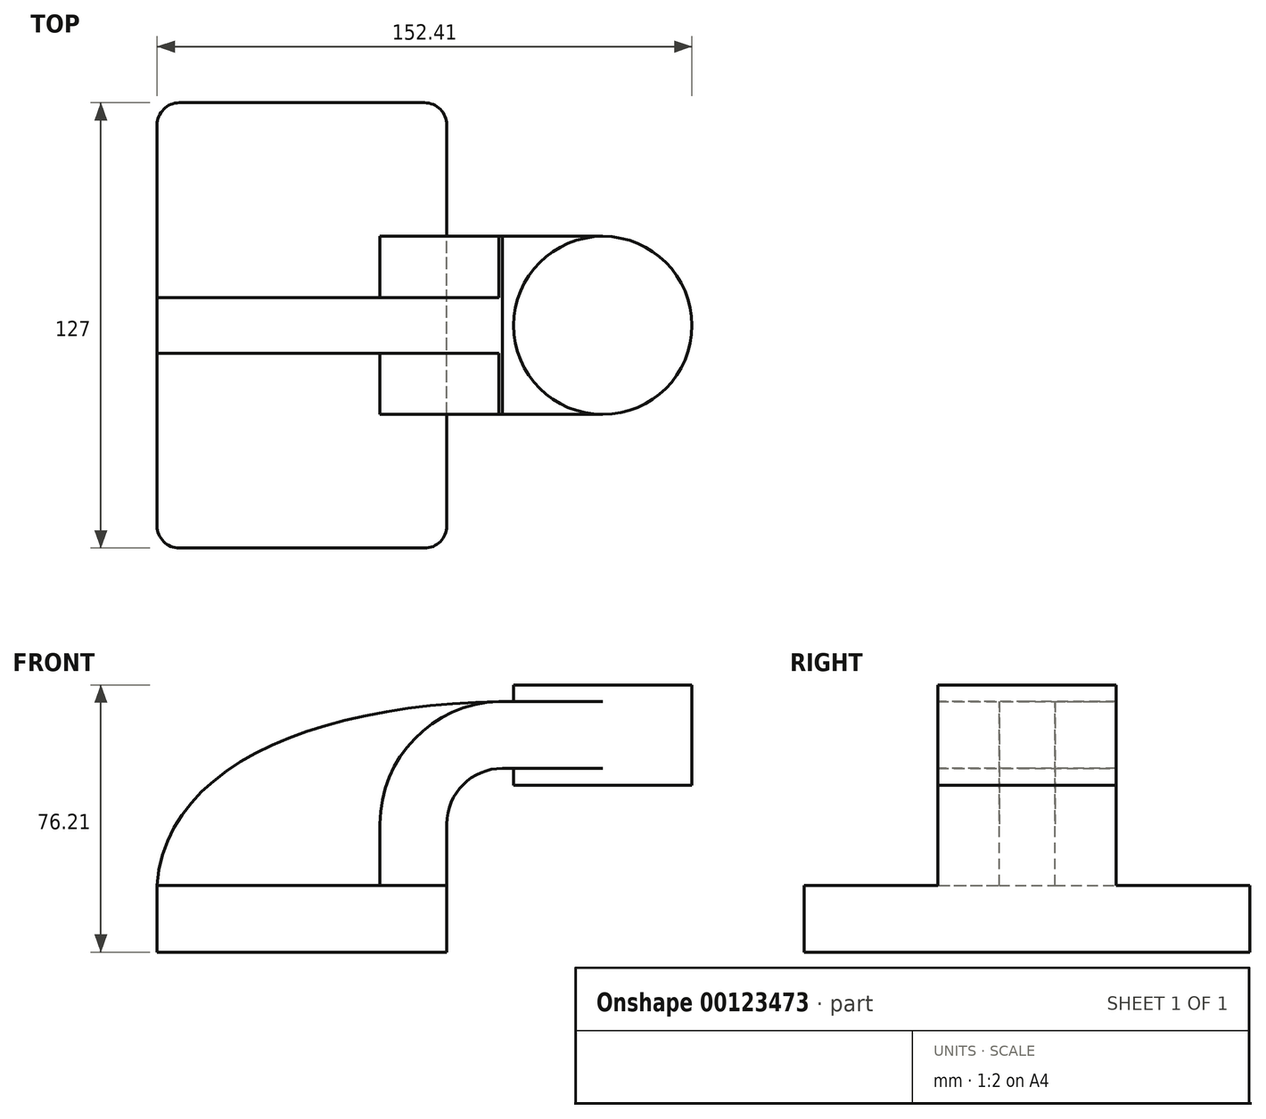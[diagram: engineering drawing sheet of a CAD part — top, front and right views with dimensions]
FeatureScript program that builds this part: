
annotation { "Feature Type Name" : "Feature", "Feature Type Description" : "" }
export const myFeature = defineFeature(function(context is Context, id is Id, definition is map)
    precondition{}
    {
        {
            var Q0;
            Q0=qCreatedBy(makeId("Front.planeOp"),FACE);
            var sketch = newSketch(context, id + "F0", { "sketchPlane" : qUnion([Q0])});
            skLineSegment(sketch, "E0.bottom", {"start": v(-41.28, 9.52) * mm, "end": v(41.28, 9.53) * mm});
            skLineSegment(sketch, "E0.top", {"start": v(-41.27, -9.52) * mm, "end": v(41.28, -9.52) * mm});
            skLineSegment(sketch, "E0.left", {"start": v(-41.28, 9.52) * mm, "end": v(-41.28, -9.52) * mm});
            skLineSegment(sketch, "E0.right", {"start": v(41.28, 9.53) * mm, "end": v(41.28, -9.52) * mm});
            skPoint(sketch, "E0.middle", {"position": v(0, 0) * mm});
            skLineSegment(sketch, "E1.bottom", {"start": v(60.33, 66.68) * mm, "end": v(111.12, 66.68) * mm});
            skLineSegment(sketch, "E1.top", {"start": v(60.32, 38.1) * mm, "end": v(111.12, 38.1) * mm});
            skLineSegment(sketch, "E1.left", {"start": v(60.33, 66.67) * mm, "end": v(60.33, 38.1) * mm});
            skLineSegment(sketch, "E1.right", {"start": v(111.12, 66.67) * mm, "end": v(111.12, 38.1) * mm});
            skPoint(sketch, "E1.middle", {"position": v(85.73, 52.39) * mm});
            skLineSegment(sketch, "E2", {"start": v(41.27, 9.53) * mm, "end": v(41.27, 27) * mm});
            skArc(sketch, "E3", {"start": v(41.27, 27) * mm, "mid": v(45.92, 38.23) * mm, "end": v(57.15, 42.88) * mm});
            skLineSegment(sketch, "E4", {"start": v(57.15, 42.88) * mm, "end": v(85.72, 42.88) * mm});
            skLineSegment(sketch, "E5.0", {"start": v(57.15, 61.93) * mm, "end": v(85.72, 61.93) * mm});
            skArc(sketch, "E5.1", {"start": v(22.22, 27) * mm, "mid": v(32.45, 51.7) * mm, "end": v(57.15, 61.93) * mm});
            skLineSegment(sketch, "E5.2", {"start": v(22.23, 9.53) * mm, "end": v(22.23, 27) * mm});
            skLineSegment(sketch, "E6", {"start": v(85.72, 38.1) * mm, "end": v(85.72, 66.68) * mm});
            skFitSpline(sketch, "E7", {"points": [v(-41.28, 9.53) * mm, v(57.15, 61.93) * mm], "startDerivative": vector(7.03, 104.38) * mm, "endDerivative": vector(154.93, 2.05) * mm});
            skSolve(sketch);
        }
        {
            var Q0;
            Q0=makeQuery(id+"F0.imprint","IMPRINT",FACE,{"disambiguationData":[TD([[makeQuery(id+"F0.imprint","IMPRINT",EDGE,{"derivedFrom":sQuery(id+"F0.wireOp",EDGE,"E0.top")}),1.0]])]});
            extrude(context, id + "F1", {"entities" : qUnion([Q0]), "endBound" : BoundingType.SYMMETRIC, "depth" : 127 * mm});
        }
        {
            var Q0;
            {var subQ1=sQuery(id+"F0.wireOp",EDGE,"E2");Q0=makeQuery(id+"F0.imprint","IMPRINT",FACE,{"disambiguationData":[TD([[makeQuery(id+"F0.imprint","IMPRINT",EDGE,{"derivedFrom":subQ1}),1.0]])]});}
            var Q1;
            {var subQ0=sQuery(id+"F0.wireOp",EDGE,"E5.0");var subQ1=sQuery(id+"F0.wireOp",EDGE,"E1.left");var subQ2=makeQuery(id+"F0.imprint","INTERSECT",VERTEX,{"derivedFrom":[subQ1,subQ0]});Q1=makeQuery(id+"F0.imprint","IMPRINT",FACE,{"disambiguationData":[TD([[makeQuery(id+"F0.imprint","IMPRINT",EDGE,{"disambiguationData":[TD([[subQ2,-1.0]])],"derivedFrom":subQ1}),1.0]])]});}
            extrude(context, id + "F2", {"entities" : qUnion([Q0, Q1]), "operationType" : NewBodyOperationType.ADD, "endBound" : BoundingType.SYMMETRIC, "depth" : 50.8 * mm});
        }
        {
            var Q0;
            {var subQ3=sQuery(id+"F0.wireOp",EDGE,"E5.2");Q0=makeQuery(id+"F0.imprint","IMPRINT",FACE,{"disambiguationData":[TD([[makeQuery(id+"F0.imprint","IMPRINT",EDGE,{"derivedFrom":subQ3}),1.0]])]});}
            extrude(context, id + "F3", {"entities" : qUnion([Q0]), "operationType" : NewBodyOperationType.ADD, "endBound" : BoundingType.SYMMETRIC, "depth" : 15.88 * mm});
        }
        {
            var Q0;
            {var subQ0=sQuery(id+"F0.wireOp",EDGE,"E1.right");Q0=makeQuery(id+"F0.imprint","IMPRINT",FACE,{"disambiguationData":[TD([[makeQuery(id+"F0.imprint","IMPRINT",EDGE,{"derivedFrom":subQ0}),-1.0]])]});}
            var Q1;
            Q1=sQuery(id+"F0.wireOp",EDGE,"E6");
            revolve(context, id + "F4", {"operationType" : NewBodyOperationType.ADD, "entities" : qUnion([Q0]), "axis" : qUnion([Q1]), "revolveType" : RevolveType.FULL});
        }
        {
            var Q0;
            Q0=makeQuery(id+"F1.opExtrude","CAP_EDGE",EDGE,{"disambiguationData":[OSD([sQuery(id+"F0.wireOp",EDGE,"E0.right")])],"isStart":false});
            var Q1;
            Q1=makeQuery(id+"F1.opExtrude","CAP_EDGE",EDGE,{"disambiguationData":[OSD([sQuery(id+"F0.wireOp",EDGE,"E0.left")])],"isStart":false});
            var Q2;
            Q2=makeQuery(id+"F1.opExtrude","CAP_EDGE",EDGE,{"disambiguationData":[OSD([sQuery(id+"F0.wireOp",EDGE,"E0.right")])],"isStart":true});
            var Q3;
            Q3=makeQuery(id+"F1.opExtrude","CAP_EDGE",EDGE,{"disambiguationData":[OSD([sQuery(id+"F0.wireOp",EDGE,"E0.left")])],"isStart":true});
            fillet(context, id + "F5", {"entities" : qUnion([Q0, Q1, Q2, Q3]), "radius" : 6.35 * mm, "tangentPropagation" : true, "allowEdgeOverflow" : false});
        }
    });
